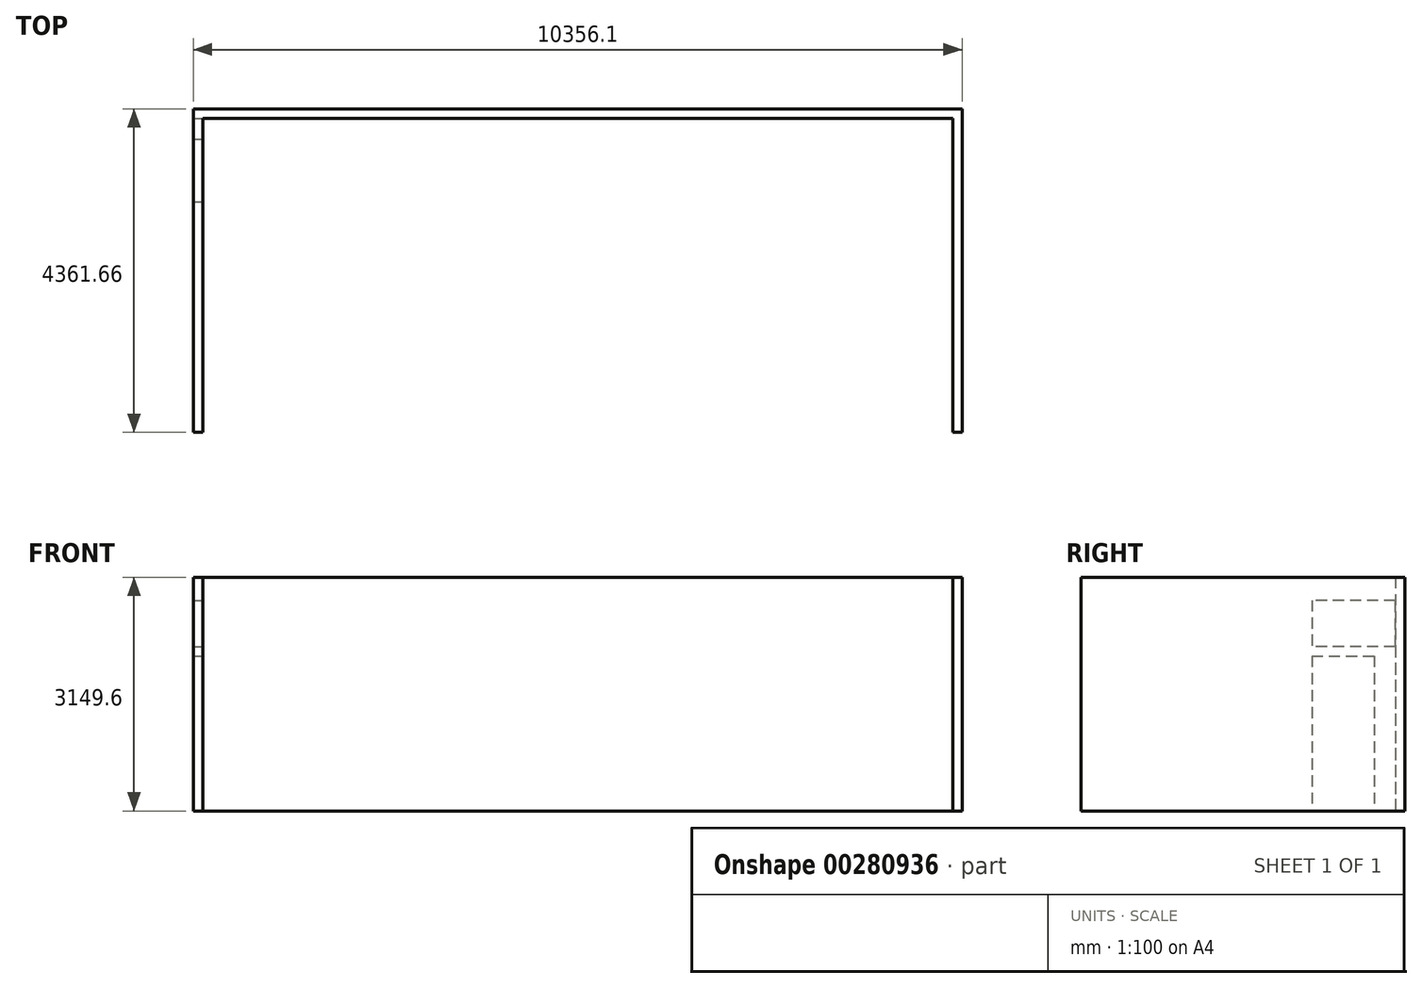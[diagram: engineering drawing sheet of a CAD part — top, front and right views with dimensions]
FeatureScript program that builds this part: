
annotation { "Feature Type Name" : "Feature", "Feature Type Description" : "" }
export const myFeature = defineFeature(function(context is Context, id is Id, definition is map)
    precondition{}
    {
        {
            var Q0;
            Q0=qCreatedBy(makeId("Top.planeOp"),FACE);
            var sketch = newSketch(context, id + "F0", { "sketchPlane" : qUnion([Q0])});
            skLineSegment(sketch, "E0.bottom", {"start": v(0, 0) * mm, "end": v(10102.06, 0) * mm});
            skLineSegment(sketch, "E0.top", {"start": v(0, 4234.66) * mm, "end": v(10102.06, 4234.66) * mm});
            skLineSegment(sketch, "E0.left", {"start": v(0, 0) * mm, "end": v(0, 4234.66) * mm});
            skLineSegment(sketch, "E0.right", {"start": v(10102.06, 0) * mm, "end": v(10102.06, 4234.66) * mm});
            skSolve(sketch);
        }
        {
            var Q0;
            Q0=makeQuery(id+"F0.imprint","IMPRINT",FACE,{"disambiguationData":[TD([[makeQuery(id+"F0.imprint","IMPRINT",EDGE,{"derivedFrom":sQuery(id+"F0.wireOp",EDGE,"E0.bottom")}),1.0]])]});
            var sketch = newSketch(context, id + "F1", { "sketchPlane" : qUnion([Q0])});
            skLineSegment(sketch, "E1.0", {"start": v(-127, 4361.66) * mm, "end": v(10229.06, 4361.66) * mm});
            skLineSegment(sketch, "E1.1", {"start": v(-127, -127) * mm, "end": v(-127, 4361.66) * mm});
            skLineSegment(sketch, "E1.2", {"start": v(-127, -127) * mm, "end": v(10229.06, -127) * mm});
            skLineSegment(sketch, "E1.3", {"start": v(10229.06, -127) * mm, "end": v(10229.06, 4361.66) * mm});
            skSolve(sketch);
        }
        {
            var Q0;
            Q0=makeQuery(id+"F1.imprint","IMPRINT",FACE,{"disambiguationData":[TD([[makeQuery(id+"F1.imprint","IMPRINT",EDGE,{"derivedFrom":sQuery(id+"F1.wireOp",EDGE,"E1.0")}),-1.0]])]});
            extrude(context, id + "F2", {"entities" : qUnion([Q0]), "depth" : 3149.6 * mm});
        }
        {
            var Q0;
            Q0=makeQuery(id+"F2.opExtrude","SWEPT_FACE",FACE,{"disambiguationData":[OSD([sQuery(id+"F0.wireOp",EDGE,"E0.left")])]});
            var sketch = newSketch(context, id + "F3", { "sketchPlane" : qUnion([Q0])});
            skLineSegment(sketch, "E2.bottom", {"start": v(4234.66, 0) * mm, "end": v(3950.5, 0) * mm, "construction": true});
            skLineSegment(sketch, "E2.top", {"start": v(4234.66, 556.25) * mm, "end": v(3950.5, 556.25) * mm, "construction": true});
            skLineSegment(sketch, "E2.left", {"start": v(4234.66, 0) * mm, "end": v(4234.66, 556.25) * mm, "construction": true});
            skLineSegment(sketch, "E2.right", {"start": v(3950.5, 0) * mm, "end": v(3950.5, 556.25) * mm, "construction": true});
            skLineSegment(sketch, "E3.bottom", {"start": v(4234.66, 0) * mm, "end": v(3110.7, 0) * mm, "construction": true});
            skLineSegment(sketch, "E3.top", {"start": v(4234.66, 556.25) * mm, "end": v(3110.7, 556.25) * mm, "construction": true});
            skLineSegment(sketch, "E3.right", {"start": v(3110.7, 0) * mm, "end": v(3110.7, 556.25) * mm, "construction": true});
            skLineSegment(sketch, "E4.bottom", {"start": v(3950.5, 0) * mm, "end": v(3110.7, 0) * mm});
            skLineSegment(sketch, "E4.top", {"start": v(3950.5, 2086.77) * mm, "end": v(3110.7, 2086.77) * mm});
            skLineSegment(sketch, "E4.left", {"start": v(3950.5, 0) * mm, "end": v(3950.5, 2086.77) * mm});
            skLineSegment(sketch, "E4.right", {"start": v(3110.7, 0) * mm, "end": v(3110.7, 2086.77) * mm});
            skSolve(sketch);
        }
        {
            var Q0;
            Q0=makeQuery(id+"F3.imprint","IMPRINT",FACE,{"disambiguationData":[TD([[makeQuery(id+"F3.imprint","IMPRINT",EDGE,{"derivedFrom":sQuery(id+"F3.wireOp",EDGE,"E4.bottom")}),1.0]])]});
            extrude(context, id + "F4", {"entities" : qUnion([Q0]), "operationType" : NewBodyOperationType.REMOVE, "endBound" : BoundingType.THROUGH_ALL, "oppositeDirection" : true, "depth" : 25.4 * mm});
        }
        {
            var Q0;
            Q0=makeQuery(id+"F2.opExtrude","SWEPT_FACE",FACE,{"disambiguationData":[OSD([sQuery(id+"F0.wireOp",EDGE,"E0.left")])]});
            var sketch = newSketch(context, id + "F5", { "sketchPlane" : qUnion([Q0])});
            skLineSegment(sketch, "E5.bottom", {"start": v(3110.7, 2086.77) * mm, "end": v(3309.59, 2086.77) * mm, "construction": true});
            skLineSegment(sketch, "E5.top", {"start": v(3110.7, 2213.77) * mm, "end": v(3309.59, 2213.77) * mm, "construction": true});
            skLineSegment(sketch, "E5.left", {"start": v(3110.7, 2086.77) * mm, "end": v(3110.7, 2213.77) * mm, "construction": true});
            skLineSegment(sketch, "E5.right", {"start": v(3309.59, 2086.77) * mm, "end": v(3309.59, 2213.77) * mm, "construction": true});
            skLineSegment(sketch, "E6.bottom", {"start": v(3110.7, 2213.77) * mm, "end": v(4279.1, 2213.77) * mm});
            skLineSegment(sketch, "E6.top", {"start": v(3110.7, 2670.97) * mm, "end": v(4279.1, 2670.97) * mm});
            skLineSegment(sketch, "E6.left", {"start": v(3110.7, 2213.77) * mm, "end": v(3110.7, 2670.97) * mm});
            skLineSegment(sketch, "E6.right", {"start": v(4279.1, 2213.77) * mm, "end": v(4279.1, 2670.97) * mm});
            skSolve(sketch);
        }
        {
            var Q0;
            {var subQ0=sQuery(id+"F5.wireOp",EDGE,"E6.left");Q0=makeQuery(id+"F5.imprint","IMPRINT",FACE,{"disambiguationData":[TD([[makeQuery(id+"F5.imprint","IMPRINT",EDGE,{"derivedFrom":subQ0}),-1.0]])]});}
            extrude(context, id + "F6", {"entities" : qUnion([Q0]), "operationType" : NewBodyOperationType.REMOVE, "endBound" : BoundingType.THROUGH_ALL, "oppositeDirection" : true, "depth" : 25.4 * mm});
        }
        {
            var Q0;
            Q0=makeQuery(id+"F2.opExtrude","SWEPT_FACE",FACE,{"disambiguationData":[OSD([sQuery(id+"F1.wireOp",EDGE,"E1.2")])]});
            extrude(context, id + "F7", {"entities" : qUnion([Q0]), "operationType" : NewBodyOperationType.REMOVE, "oppositeDirection" : true, "depth" : 127 * mm});
        }
        {
            var Q0;
            Q0=makeQuery(id+"F6.boolean.opBoolean","COPY",FACE,{"derivedFrom":makeQuery(id+"F6.opExtrude","SWEPT_FACE",FACE,{"disambiguationData":[OSD([sQuery(id+"F5.wireOp",EDGE,"E6.top")])]})});
            extrude(context, id + "F8", {"entities" : qUnion([Q0]), "operationType" : NewBodyOperationType.REMOVE, "oppositeDirection" : true, "depth" : 139.7 * mm});
        }
        {
            var Q0;
            Q0=makeQuery(id+"F8.boolean.opBoolean","COPY",FACE,{"derivedFrom":makeQuery(id+"F8.opExtrude","CAP_FACE",FACE,{"disambiguationData":[OSD([sQuery(id+"F5.wireOp",EDGE,"E6.top")])],"isStart":false})});
            extrude(context, id + "F9", {"entities" : qUnion([Q0]), "operationType" : NewBodyOperationType.REMOVE, "oppositeDirection" : true, "depth" : 25.4 * mm});
        }
    });
